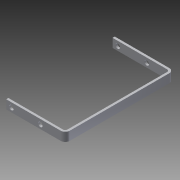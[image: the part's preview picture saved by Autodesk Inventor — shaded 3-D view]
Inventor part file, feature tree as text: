
AUTODESK INVENTOR PART (.ipt)
format: ipt  version: 2013 (Build 170138000, 138)  size: 117,248 bytes
history: native  units: in
note: dims shown in document units (in); Inventor stores cm internally (conversion verified against a paired STEP export)
features: sheet_metal_op x7, other x3, sketch x3, reference x2, extrude x1
ambient origin geometry x8: Origin, YZ Plane, XZ Plane, XY Plane, X Axis, Y Axis, Z Axis, Center Point
feature tree (16):
  sheet_metal_op  "Face2"
  sheet_metal_op  "Flange4"
  sheet_metal_op  "Flange5"
  extrude  "Extrusion2"  Depth=0.5in
  other  "Plate5"
  sketch  "Sketch6"  dims[d1=3.119in d2=0.5in]
  other  "Plate6"
  sheet_metal_op  "Bend4"
  sheet_metal_op  "Corner4"
  sketch  "Sketch7"  dims[d5=0.295in]
  other  "Plate7"
  sheet_metal_op  "Bend5"
  sheet_metal_op  "Corner5"
  sketch  "Sketch8"  dims[d8=0.125in d42=0.125in d43=0.125in d44=0.0625in d45=0.25in d46=0.125in d47=5.947in d48=90.0deg d49=0.125in d50=0.5in d51=0.125in d52=0.125in d53=0.125in d54=0.0625in d55=0.25in d56=0.125in d57=3.369in d58=90.0deg d59=0.125in d60=0.5in d61=0.125in d62=0.125in d63=99999.0in d64=0.0in]
  reference  "Reference1"
  reference  "Reference2"
